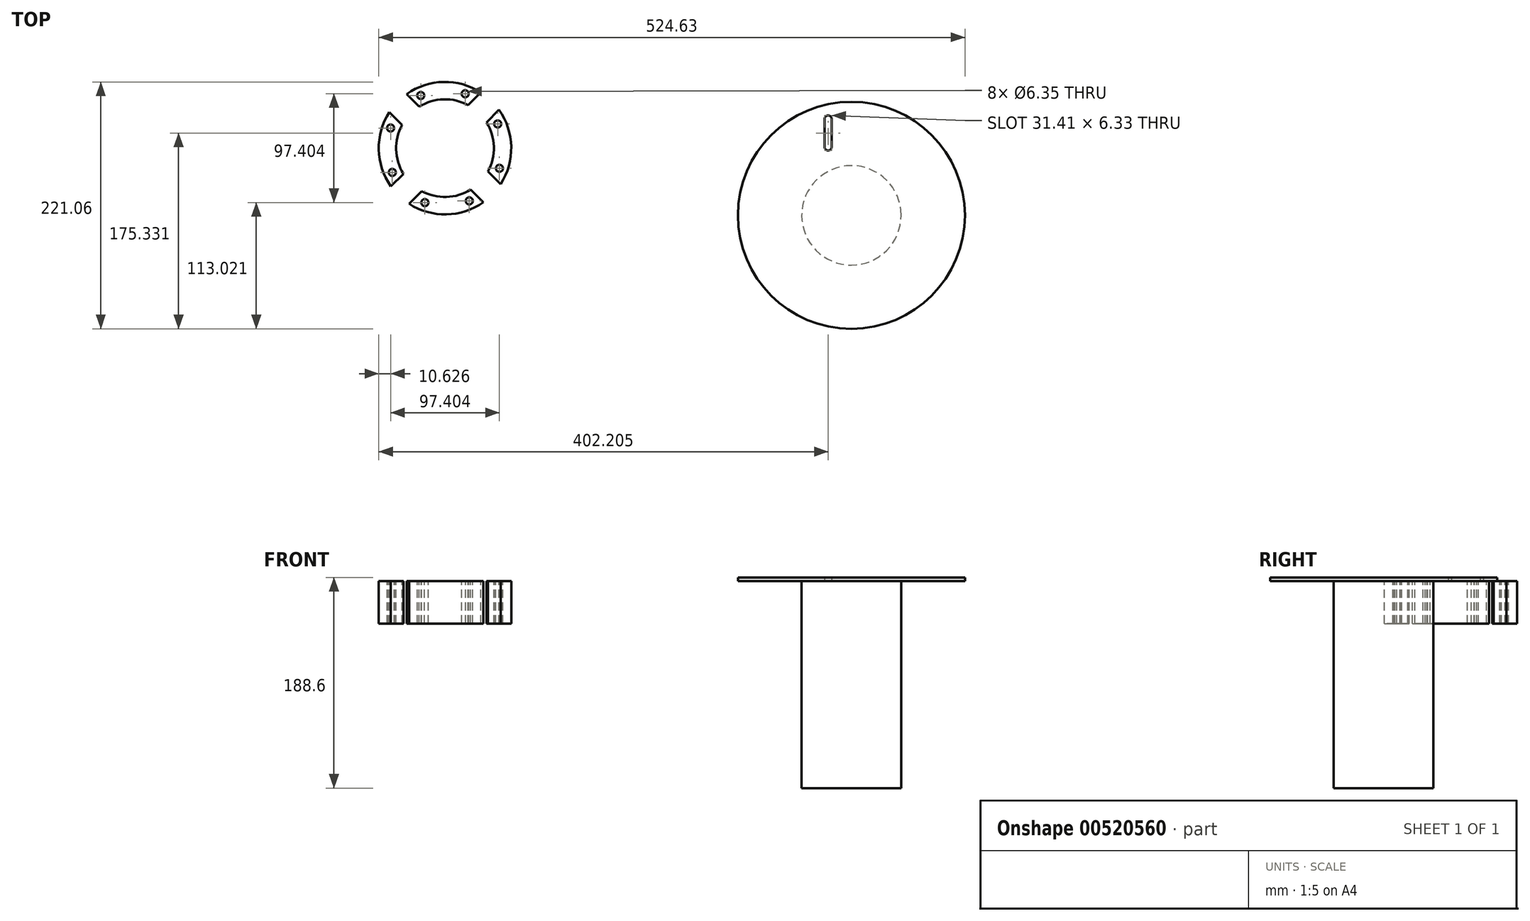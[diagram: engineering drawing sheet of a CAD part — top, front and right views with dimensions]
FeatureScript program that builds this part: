
annotation { "Feature Type Name" : "Feature", "Feature Type Description" : "" }
export const myFeature = defineFeature(function(context is Context, id is Id, definition is map)
    precondition{}
    {
        {
            var Q0;
            Q0=qCreatedBy(makeId("Top.planeOp"),FACE);
            var sketch = newSketch(context, id + "F0", { "sketchPlane" : qUnion([Q0])});
            skCircle(sketch, "E0", {"center": v(0, 0) * mm, "radius": 44.51 * mm});
            skSolve(sketch);
        }
        {
            var Q0;
            Q0=makeQuery(id+"F0.imprint","IMPRINT",FACE,{"disambiguationData":[TD([[makeQuery(id+"F0.imprint","IMPRINT",EDGE,{"derivedFrom":sQuery(id+"F0.wireOp",EDGE,"E0")}),1.0]])]});
            extrude(context, id + "F1", {"entities" : qUnion([Q0]), "oppositeDirection" : true, "depth" : 185.42 * mm, "offsetDistance" : 25.4 * mm});
        }
        {
            var Q0;
            Q0=qCreatedBy(makeId("Top.planeOp"),FACE);
            var sketch = newSketch(context, id + "F2", { "sketchPlane" : qUnion([Q0])});
            skCircle(sketch, "E1", {"center": v(0, 0) * mm, "radius": 101.6 * mm});
            skLineSegment(sketch, "E2.left", {"start": v(-24, 86.6) * mm, "end": v(-24, 61.2) * mm});
            skLineSegment(sketch, "E2.right", {"start": v(-17.66, 86.27) * mm, "end": v(-17.66, 60.87) * mm});
            skArc(sketch, "E3", {"start": v(-24, 61.2) * mm, "mid": v(-20.98, 58.02) * mm, "end": v(-17.66, 60.87) * mm});
            skArc(sketch, "E4", {"start": v(-17.66, 86.27) * mm, "mid": v(-20.67, 89.44) * mm, "end": v(-24, 86.6) * mm});
            skSolve(sketch);
        }
        {
            var Q0;
            Q0=makeQuery(id+"F2.imprint","IMPRINT",FACE,{"disambiguationData":[TD([[makeQuery(id+"F2.imprint","IMPRINT",EDGE,{"derivedFrom":sQuery(id+"F2.wireOp",EDGE,"E1")}),1.0]])]});
            extrude(context, id + "F3", {"entities" : qUnion([Q0]), "depth" : 3.17 * mm, "offsetDistance" : 25.4 * mm});
        }
        {
            var Q0;
            Q0=qCreatedBy(makeId("Top.planeOp"),FACE);
            var sketch = newSketch(context, id + "F4", { "sketchPlane" : qUnion([Q0])});
            skLineSegment(sketch, "E5", {"start": v(-412.12, 25.87) * mm, "end": v(-400.88, 37.11) * mm});
            skArc(sketch, "E6", {"start": v(-412.03, 25.74) * mm, "mid": v(-423.01, 58.79) * mm, "end": v(-413.56, 92.3) * mm});
            skArc(sketch, "E7", {"start": v(-400.8, 36.97) * mm, "mid": v(-407.43, 58.77) * mm, "end": v(-402.2, 80.95) * mm});
            skLineSegment(sketch, "E8", {"start": v(-413.56, 92.3) * mm, "end": v(-402.2, 80.95) * mm});
            skLineSegment(sketch, "E9.1.0", {"start": v(-398, 108.55) * mm, "end": v(-386.75, 97.3) * mm});
            skArc(sketch, "E9.1.1", {"start": v(-398.12, 108.46) * mm, "mid": v(-365.08, 119.44) * mm, "end": v(-331.56, 109.98) * mm});
            skArc(sketch, "E9.1.2", {"start": v(-386.9, 97.22) * mm, "mid": v(-365.1, 103.86) * mm, "end": v(-342.92, 98.63) * mm});
            skLineSegment(sketch, "E9.1.3", {"start": v(-331.56, 109.98) * mm, "end": v(-342.92, 98.63) * mm});
            skLineSegment(sketch, "E9.2.0", {"start": v(-315.32, 94.42) * mm, "end": v(-326.56, 83.18) * mm});
            skArc(sketch, "E9.2.1", {"start": v(-315.4, 94.55) * mm, "mid": v(-304.42, 61.5) * mm, "end": v(-313.88, 28) * mm});
            skArc(sketch, "E9.2.2", {"start": v(-326.64, 83.32) * mm, "mid": v(-320, 61.52) * mm, "end": v(-325.24, 39.35) * mm});
            skLineSegment(sketch, "E9.2.3", {"start": v(-313.88, 28) * mm, "end": v(-325.24, 39.35) * mm});
            skLineSegment(sketch, "E9.3.0", {"start": v(-329.44, 11.74) * mm, "end": v(-340.68, 22.99) * mm});
            skArc(sketch, "E9.3.1", {"start": v(-329.31, 11.83) * mm, "mid": v(-362.36, 0.85) * mm, "end": v(-395.87, 10.3) * mm});
            skArc(sketch, "E9.3.2", {"start": v(-340.55, 23.07) * mm, "mid": v(-362.34, 16.43) * mm, "end": v(-384.52, 21.66) * mm});
            skLineSegment(sketch, "E9.3.3", {"start": v(-395.87, 10.3) * mm, "end": v(-384.52, 21.66) * mm});
            skCircle(sketch, "E10", {"center": v(-412.4, 78.14) * mm, "radius": 3.18 * mm});
            skCircle(sketch, "E11.1.0", {"center": v(-410.88, 38.42) * mm, "radius": 3.17 * mm});
            skCircle(sketch, "E11.2.0", {"center": v(-381.72, 11.42) * mm, "radius": 3.17 * mm});
            skCircle(sketch, "E11.3.0", {"center": v(-342, 12.95) * mm, "radius": 3.17 * mm});
            skCircle(sketch, "E11.4.0", {"center": v(-315, 42.1) * mm, "radius": 3.17 * mm});
            skCircle(sketch, "E11.5.0", {"center": v(-316.53, 81.82) * mm, "radius": 3.17 * mm});
            skCircle(sketch, "E11.6.0", {"center": v(-345.69, 108.83) * mm, "radius": 3.17 * mm});
            skCircle(sketch, "E11.7.0", {"center": v(-385.4, 107.3) * mm, "radius": 3.18 * mm});
            skSolve(sketch);
        }
        {
            var Q0;
            Q0 = qSketchRegion(id + "F4", true);
            extrude(context, id + "F5", {"entities" : qUnion([Q0]), "oppositeDirection" : true, "depth" : 38.1 * mm, "offsetDistance" : 25.4 * mm});
        }
    });
